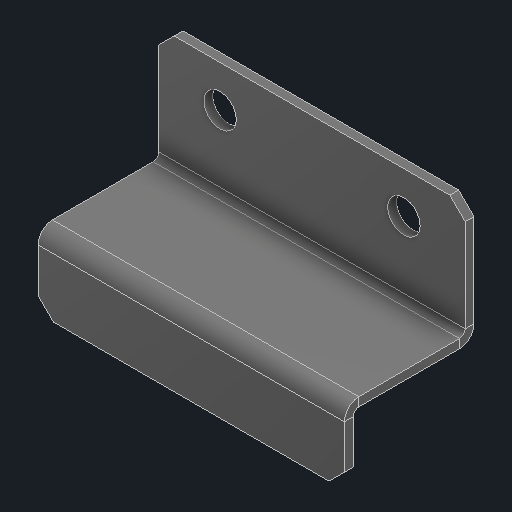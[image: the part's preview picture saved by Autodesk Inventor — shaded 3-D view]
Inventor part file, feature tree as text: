
AUTODESK INVENTOR PART (.ipt)
format: ipt  version: 2024 (Build 280153000, 153)  size: 124,416 bytes
history: native  units: in
note: dims shown in document units (in); Inventor stores cm internally (conversion verified against a paired STEP export)
features: chamfer x1
ambient origin geometry x8: Origin, YZ Plane, XZ Plane, XY Plane, X Axis, Y Axis, Z Axis, Center Point
bodies: Solid1 (feature_tree)
feature tree (1):
  chamfer  "Chamfer1"  [1 undecoded]
note: 1 required parameter value undecoded (feature->parameter linkage not recoverable at this tier; creation-order binding heuristic only, values carry confidence <= 0.55)
